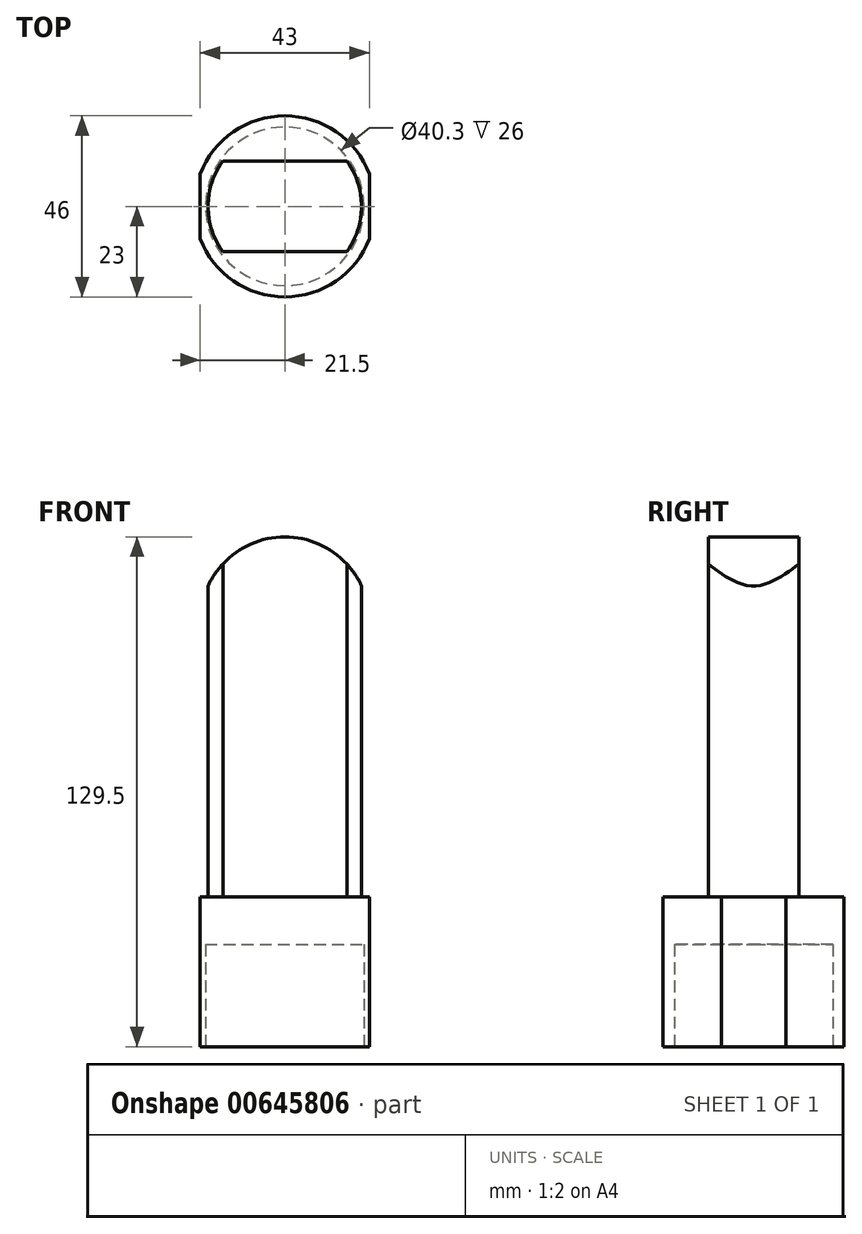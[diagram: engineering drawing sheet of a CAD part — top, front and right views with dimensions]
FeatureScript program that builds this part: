
annotation { "Feature Type Name" : "Feature", "Feature Type Description" : "" }
export const myFeature = defineFeature(function(context is Context, id is Id, definition is map)
    precondition{}
    {
        {
            var Q0;
            Q0=qCreatedBy(makeId("Top.planeOp"),FACE);
            var sketch = newSketch(context, id + "F0", { "sketchPlane" : qUnion([Q0])});
            skCircle(sketch, "E0", {"center": v(0, 0) * mm, "radius": 23 * mm});
            skLineSegment(sketch, "E1", {"start": v(-21.5, 8.17) * mm, "end": v(-21.5, -8.17) * mm});
            skLineSegment(sketch, "E2.MirrorCS", {"start": v(21.5, 8.17) * mm, "end": v(21.5, -8.17) * mm});
            skSolve(sketch);
        }
        {
            var Q0;
            {var subQ0=sQuery(id+"F0.wireOp",EDGE,"E1");Q0=makeQuery(id+"F0.imprint","IMPRINT",FACE,{"disambiguationData":[TD([[makeQuery(id+"F0.imprint","IMPRINT",EDGE,{"derivedFrom":subQ0}),1.0]])]});}
            extrude(context, id + "F1", {"entities" : qUnion([Q0]), "depth" : 38 * mm, "offsetDistance" : 25 * mm});
        }
        {
            var Q0;
            Q0=makeQuery(id+"F1.opExtrude","CAP_FACE",FACE,{"disambiguationData":[OSD([sQuery(id+"F0.wireOp",EDGE,"E0"),sQuery(id+"F0.wireOp",EDGE,"E1"),sQuery(id+"F0.wireOp",EDGE,"E2.MirrorCS")])],"isStart":true});
            var sketch = newSketch(context, id + "F2", { "sketchPlane" : qUnion([Q0])});
            skCircle(sketch, "E3", {"center": v(0, 0) * mm, "radius": 20.15 * mm});
            skSolve(sketch);
        }
        {
            var Q0;
            Q0 = qSketchRegion(id + "F2", true);
            extrude(context, id + "F3", {"entities" : qUnion([Q0]), "operationType" : NewBodyOperationType.REMOVE, "oppositeDirection" : true, "depth" : 26 * mm, "offsetDistance" : 25 * mm});
        }
        {
            var Q0;
            Q0=makeQuery(id+"F1.opExtrude","CAP_FACE",FACE,{"disambiguationData":[OSD([sQuery(id+"F0.wireOp",EDGE,"E0"),sQuery(id+"F0.wireOp",EDGE,"E1"),sQuery(id+"F0.wireOp",EDGE,"E2.MirrorCS")])],"isStart":false});
            var sketch = newSketch(context, id + "F4", { "sketchPlane" : qUnion([Q0])});
            skCircle(sketch, "E4", {"center": v(0, 0) * mm, "radius": 19.5 * mm});
            skLineSegment(sketch, "E5", {"start": v(-15.75, 11.5) * mm, "end": v(15.75, 11.5) * mm});
            skLineSegment(sketch, "E6.MirrorCS", {"start": v(-15.75, -11.5) * mm, "end": v(15.75, -11.5) * mm});
            skSolve(sketch);
        }
        {
            var Q0;
            {var subQ0=sQuery(id+"F4.wireOp",EDGE,"E5");Q0=makeQuery(id+"F4.imprint","IMPRINT",FACE,{"disambiguationData":[TD([[makeQuery(id+"F4.imprint","IMPRINT",EDGE,{"derivedFrom":subQ0}),-1.0]])]});}
            extrude(context, id + "F5", {"entities" : qUnion([Q0]), "operationType" : NewBodyOperationType.ADD, "depth" : 93 * mm, "offsetDistance" : 25 * mm});
        }
        {
            var Q0;
            Q0=makeQuery(id+"F5.opExtrude","SWEPT_FACE",FACE,{"disambiguationData":[OSD([sQuery(id+"F4.wireOp",EDGE,"E6.MirrorCS")])]});
            var sketch = newSketch(context, id + "F6", { "sketchPlane" : qUnion([Q0])});
            skCircle(sketch, "E7", {"center": v(0, 108) * mm, "radius": 21.5 * mm});
            skLineSegment(sketch, "E8", {"start": v(-20.67, 113.9) * mm, "end": v(-34.22, 134.26) * mm});
            skLineSegment(sketch, "E9", {"start": v(-34.22, 134.26) * mm, "end": v(30.43, 134.26) * mm});
            skLineSegment(sketch, "E10", {"start": v(30.43, 134.26) * mm, "end": v(20.96, 112.77) * mm});
            skSolve(sketch);
        }
        {
            var Q0;
            {var subQ0=sQuery(id+"F6.wireOp",EDGE,"E8");Q0=makeQuery(id+"F6.imprint","IMPRINT",FACE,{"disambiguationData":[TD([[makeQuery(id+"F6.imprint","IMPRINT",EDGE,{"derivedFrom":subQ0}),-1.0]])]});}
            var Q1;
            {var subQ1=sQuery(id+"F4.wireOp",EDGE,"E6.MirrorCS");var subQ7=makeQuery(id+"F5.opExtrude","CAP_EDGE",EDGE,{"disambiguationData":[OSD([subQ1])],"isStart":false});Q1=makeQuery(id+"F6.imprint","IMPRINT",FACE,{"disambiguationData":[TD([[makeQuery(id+"F6.imprint","IMPRINT",EDGE,{"derivedFrom":subQ7}),-1.0]])]});}
            extrude(context, id + "F7", {"entities" : qUnion([Q0, Q1]), "operationType" : NewBodyOperationType.REMOVE, "oppositeDirection" : true, "depth" : 25 * mm, "offsetDistance" : 25 * mm});
        }
    });
